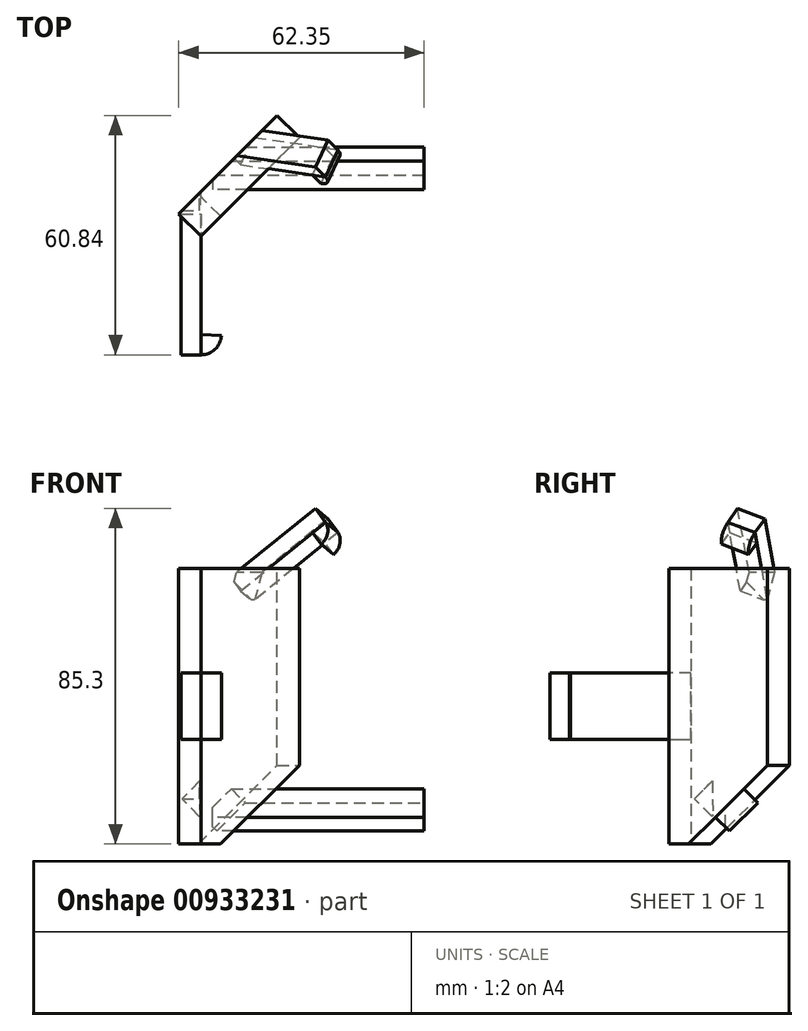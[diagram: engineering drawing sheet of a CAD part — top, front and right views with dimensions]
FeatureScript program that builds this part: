
annotation { "Feature Type Name" : "Feature", "Feature Type Description" : "" }
export const myFeature = defineFeature(function(context is Context, id is Id, definition is map)
    precondition{}
    {
        {
            var Q0;
            Q0=qCreatedBy(makeId("Top.planeOp"),FACE);
            var sketch = newSketch(context, id + "F0", { "sketchPlane" : qUnion([Q0])});
            skLineSegment(sketch, "E0.bottom", {"start": v(-25, 25) * mm, "end": v(25, 25) * mm});
            skLineSegment(sketch, "E0.top", {"start": v(-25, -25) * mm, "end": v(25, -25) * mm});
            skLineSegment(sketch, "E0.left", {"start": v(-25, 25) * mm, "end": v(-25, -25) * mm});
            skLineSegment(sketch, "E0.right", {"start": v(25, 25) * mm, "end": v(25, -25) * mm});
            skPoint(sketch, "E1", {"position": v(0, 25) * mm});
            skPoint(sketch, "E2", {"position": v(25, 0) * mm});
            skSolve(sketch);
        }
        {
            var Q0;
            Q0=qSketchRegion(id+"F0",true);
            extrude(context, id + "F1", {"entities" : qUnion([Q0]), "depth" : 80 * mm, "offsetDistance" : 25 * mm});
        }
        {
            var Q0;
            Q0=makeQuery(id+"F1.opExtrude","SWEPT_EDGE",EDGE,{"disambiguationData":[OSD([sQuery(id+"F0.wireOp",EDGE,"E0.top"),sQuery(id+"F0.wireOp",EDGE,"E0.right")])]});
            var Q1;
            Q1=makeQuery(id+"F1.opExtrude","CAP_EDGE",EDGE,{"disambiguationData":[OSD([sQuery(id+"F0.wireOp",EDGE,"E0.right")])],"isStart":false});
            var Q2;
            Q2=makeQuery(id+"F1.opExtrude","CAP_EDGE",EDGE,{"disambiguationData":[OSD([sQuery(id+"F0.wireOp",EDGE,"E0.top")])],"isStart":false});
            chamfer(context, id + "F2", {"entities" : qUnion([Q0, Q1, Q2]), "chamferType" : ChamferType.OFFSET_ANGLE, "width" : 20 * mm, "oppositeDirection" : false, "angle" : 50 * degree, "tangentPropagation" : true});
        }
        {
            var Q0;
            Q0=makeQuery(id+"F1.opExtrude","SWEPT_EDGE",EDGE,{"disambiguationData":[OSD([sQuery(id+"F0.wireOp",EDGE,"E0.bottom"),sQuery(id+"F0.wireOp",EDGE,"E0.left")])]});
            chamfer(context, id + "F3", {"entities" : qUnion([Q0]), "width" : 25 * mm, "tangentPropagation" : true});
        }
        {
            var Q0;
            {var subQ0=sQuery(id+"F0.wireOp",EDGE,"E0.left");var subQ1=sQuery(id+"F0.wireOp",EDGE,"E0.bottom");Q0=makeQuery(id+"F3.opChamfer","BLEND_EDGE",EDGE,{"blendedFrom":[makeQuery(id+"F1.opExtrude","SWEPT_EDGE",EDGE,{"disambiguationData":[OSD([subQ1,subQ0])]}),makeQuery(id+"F1.opExtrude","CAP_FACE",FACE,{"disambiguationData":[OSD([subQ1,sQuery(id+"F0.wireOp",EDGE,"E0.top"),subQ0,sQuery(id+"F0.wireOp",EDGE,"E0.right")])],"isStart":false})],"blendedInto":[makeQuery(id+"F1.opExtrude","CAP_FACE",FACE,{"disambiguationData":[OSD([subQ1,sQuery(id+"F0.wireOp",EDGE,"E0.top"),subQ0,sQuery(id+"F0.wireOp",EDGE,"E0.right")])],"isStart":false})]});}
            chamfer(context, id + "F4", {"entities" : qUnion([Q0]), "width" : 10 * mm, "tangentPropagation" : true});
        }
        {
            var Q0;
            Q0=makeQuery(id+"F1.opExtrude","CAP_EDGE",EDGE,{"disambiguationData":[OSD([sQuery(id+"F0.wireOp",EDGE,"E0.bottom")])],"isStart":true});
            var Q1;
            Q1=makeQuery(id+"F1.opExtrude","CAP_EDGE",EDGE,{"disambiguationData":[OSD([sQuery(id+"F0.wireOp",EDGE,"E0.top")])],"isStart":true});
            chamfer(context, id + "F5", {"entities" : qUnion([Q0, Q1]), "width" : 20 * mm, "tangentPropagation" : true});
        }
        {
            var Q0;
            Q0=makeQuery(id+"F3.opChamfer","BLEND_FACE",FACE,{"disambiguationData":[OSD([sQuery(id+"F0.wireOp",EDGE,"E0.bottom"),sQuery(id+"F0.wireOp",EDGE,"E0.left")])]});
            var sketch = newSketch(context, id + "F6", { "sketchPlane" : qUnion([Q0])});
            skLineSegment(sketch, "E3", {"start": v(17.68, 70) * mm, "end": v(17.68, 0) * mm});
            skLineSegment(sketch, "E4", {"start": v(17.68, 0) * mm, "end": v(10.6, 0) * mm});
            skLineSegment(sketch, "E5", {"start": v(10.6, 0) * mm, "end": v(-17.68, 20) * mm});
            skLineSegment(sketch, "E6", {"start": v(-17.68, 20) * mm, "end": v(-17.68, 70) * mm});
            skLineSegment(sketch, "E7", {"start": v(-17.68, 70) * mm, "end": v(17.68, 70) * mm});
            skSolve(sketch);
        }
        {
            var Q0;
            Q0=makeQuery(id+"F6.imprint","IMPRINT",FACE,{"disambiguationData":[TD([[makeQuery(id+"F6.imprint","IMPRINT",EDGE,{"derivedFrom":sQuery(id+"F6.wireOp",EDGE,"E3")}),-1.0]])]});
            cPlane(context, id + "F7", {"entities" : qUnion([Q0]), "cplaneType" : CPlaneType.OFFSET, "offset" : 0 * mm, "width" : 150 * mm, "height" : 150 * mm});
        }
        {
            var Q0;
            Q0=qCreatedBy(id+"F7.planeOp",FACE);
            var sketch = newSketch(context, id + "F8", { "sketchPlane" : qUnion([Q0])});
            skLineSegment(sketch, "E8", {"start": v(17.68, 70) * mm, "end": v(17.68, 0) * mm});
            skLineSegment(sketch, "E9", {"start": v(17.68, 0) * mm, "end": v(10.6, 0) * mm});
            skLineSegment(sketch, "E10", {"start": v(10.6, 0) * mm, "end": v(-17.68, 20) * mm});
            skLineSegment(sketch, "E11", {"start": v(-17.68, 20) * mm, "end": v(-17.68, 70) * mm});
            skLineSegment(sketch, "E12", {"start": v(-17.68, 70) * mm, "end": v(17.68, 70) * mm});
            skSolve(sketch);
        }
        {
            var Q0;
            Q0=qSketchRegion(id+"F8",true);
            extrude(context, id + "F9", {"entities" : qUnion([Q0]), "depth" : 8 * mm, "offsetDistance" : 25 * mm});
        }
        {
            var Q0;
            Q0=makeQuery(id+"F4.opChamfer","BLEND_FACE",FACE,{"disambiguationData":[OSD([sQuery(id+"F0.wireOp",EDGE,"E0.bottom"),sQuery(id+"F0.wireOp",EDGE,"E0.top"),sQuery(id+"F0.wireOp",EDGE,"E0.left"),sQuery(id+"F0.wireOp",EDGE,"E0.right")])]});
            cPlane(context, id + "F10", {"entities" : qUnion([Q0]), "cplaneType" : CPlaneType.OFFSET, "offset" : 0 * mm, "width" : 150 * mm, "height" : 150 * mm});
        }
        {
            var Q0;
            Q0=qCreatedBy(id+"F10.planeOp",FACE);
            var sketch = newSketch(context, id + "F11", { "sketchPlane" : qUnion([Q0])});
            skLineSegment(sketch, "E13", {"start": v(13.4, -29.38) * mm, "end": v(29.08, -48.84) * mm});
            skLineSegment(sketch, "E14", {"start": v(29.08, -48.84) * mm, "end": v(38.48, -41.27) * mm});
            skLineSegment(sketch, "E15", {"start": v(38.48, -41.27) * mm, "end": v(22.8, -21.8) * mm});
            skLineSegment(sketch, "E16", {"start": v(13.4, -29.38) * mm, "end": v(22.8, -21.8) * mm});
            skPoint(sketch, "E17", {"position": v(18.1, -25.59) * mm});
            skSolve(sketch);
        }
        {
            var Q0;
            Q0=makeQuery(id+"F1.opExtrude","SWEPT_FACE",FACE,{"disambiguationData":[OSD([sQuery(id+"F0.wireOp",EDGE,"E0.left")])]});
            cPlane(context, id + "F12", {"entities" : qUnion([Q0]), "cplaneType" : CPlaneType.OFFSET, "offset" : 0 * mm, "width" : 150 * mm, "height" : 150 * mm});
        }
        {
            var Q0;
            Q0=qCreatedBy(id+"F12.planeOp",FACE);
            var sketch = newSketch(context, id + "F13", { "sketchPlane" : qUnion([Q0])});
            skLineSegment(sketch, "E18", {"start": v(-5.66, 43.45) * mm, "end": v(30.18, 43.45) * mm});
            skLineSegment(sketch, "E19", {"start": v(30.18, 43.45) * mm, "end": v(30.18, 26.55) * mm});
            skLineSegment(sketch, "E20", {"start": v(30.18, 26.55) * mm, "end": v(-5.66, 26.55) * mm});
            skLineSegment(sketch, "E21", {"start": v(-5.66, 26.55) * mm, "end": v(-5.66, 43.45) * mm});
            skPoint(sketch, "E22", {"position": v(-5.66, 35) * mm});
            skSolve(sketch);
        }
        {
            var Q0;
            Q0=qSketchRegion(id+"F13",true);
            extrude(context, id + "F14", {"entities" : qUnion([Q0]), "depth" : 5 * mm, "offsetDistance" : 25 * mm});
        }
        {
            var Q0;
            Q0=makeQuery(id+"F1.opExtrude","CAP_FACE",FACE,{"disambiguationData":[OSD([sQuery(id+"F0.wireOp",EDGE,"E0.bottom"),sQuery(id+"F0.wireOp",EDGE,"E0.top"),sQuery(id+"F0.wireOp",EDGE,"E0.left"),sQuery(id+"F0.wireOp",EDGE,"E0.right")])],"isStart":true});
            cPlane(context, id + "F15", {"entities" : qUnion([Q0]), "cplaneType" : CPlaneType.OFFSET, "offset" : 0 * mm, "width" : 150 * mm, "height" : 150 * mm});
        }
        {
            var Q0;
            Q0=qCreatedBy(id+"F15.planeOp",FACE);
            var sketch = newSketch(context, id + "F16", { "sketchPlane" : qUnion([Q0])});
            skLineSegment(sketch, "E23", {"start": v(-30.03, -6.76) * mm, "end": v(-14.64, 9.79) * mm});
            skLineSegment(sketch, "E24", {"start": v(-30.03, -6.76) * mm, "end": v(-25.94, -10.56) * mm});
            skLineSegment(sketch, "E25", {"start": v(-25.94, -10.56) * mm, "end": v(-10.56, 5.99) * mm});
            skLineSegment(sketch, "E26", {"start": v(-10.56, 5.99) * mm, "end": v(-14.64, 9.79) * mm});
            skSolve(sketch);
        }
        {
            var Q0;
            Q0=makeQuery(id+"F5.opChamfer","BLEND_FACE",FACE,{"disambiguationData":[OSD([sQuery(id+"F0.wireOp",EDGE,"E0.bottom")])]});
            var sketch = newSketch(context, id + "F17", { "sketchPlane" : qUnion([Q0])});
            skLineSegment(sketch, "E27", {"start": v(22, 23.4) * mm, "end": v(-31.69, 23.4) * mm});
            skLineSegment(sketch, "E28", {"start": v(-31.69, 23.4) * mm, "end": v(-31.69, 13.2) * mm});
            skLineSegment(sketch, "E29", {"start": v(-31.69, 13.2) * mm, "end": v(22, 13.2) * mm});
            skLineSegment(sketch, "E30", {"start": v(22, 13.2) * mm, "end": v(22, 23.4) * mm});
            skSolve(sketch);
        }
        {
            var Q0;
            Q0=qSketchRegion(id+"F17",true);
            extrude(context, id + "F18", {"entities" : qUnion([Q0]), "depth" : 5 * mm, "offsetDistance" : 25 * mm});
        }
        {
            var Q0;
            Q0=makeQuery(id+"F14.opExtrude","SWEPT_FACE",FACE,{"disambiguationData":[OSD([sQuery(id+"F13.wireOp",EDGE,"E20")])]});
            var sketch = newSketch(context, id + "F19", { "sketchPlane" : qUnion([Q0])});
            skArc(sketch, "E31", {"start": v(-19.8, 25.22) * mm, "mid": v(-21.4, 28.74) * mm, "end": v(-25, 30.18) * mm});
            skLineSegment(sketch, "E32", {"start": v(-25, 30.18) * mm, "end": v(-25, 24.96) * mm});
            skLineSegment(sketch, "E33", {"start": v(-19.8, 25.22) * mm, "end": v(-25, 24.96) * mm});
            skSolve(sketch);
        }
        {
            var Q0;
            Q0=qSketchRegion(id+"F19",true);
            extrude(context, id + "F20", {"entities" : qUnion([Q0]), "oppositeDirection" : true, "depth" : 17 * mm, "offsetDistance" : 25 * mm});
        }
        {
            var Q0;
            Q0=makeQuery(id+"F9.opExtrude","CAP_FACE",FACE,{"disambiguationData":[OSD([sQuery(id+"F8.wireOp",EDGE,"E8"),sQuery(id+"F8.wireOp",EDGE,"E9"),sQuery(id+"F8.wireOp",EDGE,"E10"),sQuery(id+"F8.wireOp",EDGE,"E11"),sQuery(id+"F8.wireOp",EDGE,"E12")])],"isStart":false});
            var sketch = newSketch(context, id + "F21", { "sketchPlane" : qUnion([Q0])});
            skLineSegment(sketch, "E34", {"start": v(6.42, 2.96) * mm, "end": v(-6.89, 12.37) * mm});
            skLineSegment(sketch, "E35", {"start": v(-6.89, 12.37) * mm, "end": v(4.32, 20) * mm});
            skLineSegment(sketch, "E36", {"start": v(4.32, 20) * mm, "end": v(6.42, 2.96) * mm});
            skSolve(sketch);
        }
        {
            var Q0;
            Q0=qSketchRegion(id+"F21",true);
            extrude(context, id + "F22", {"entities" : qUnion([Q0]), "operationType" : NewBodyOperationType.REMOVE, "endBound" : BoundingType.THROUGH_ALL, "depth" : 25 * mm, "offsetDistance" : 25 * mm});
        }
        {
            var Q0;
            Q0=makeQuery(id+"F18.opExtrude","SWEPT_FACE",FACE,{"disambiguationData":[OSD([sQuery(id+"F17.wireOp",EDGE,"E27")])]});
            var sketch = newSketch(context, id + "F23", { "sketchPlane" : qUnion([Q0])});
            skArc(sketch, "E37", {"start": v(25.12, -2.7) * mm, "mid": v(29.65, -0.94) * mm, "end": v(31.53, 3.54) * mm});
            skLineSegment(sketch, "E38", {"start": v(31.53, 3.54) * mm, "end": v(25.3, 3.53) * mm});
            skLineSegment(sketch, "E39", {"start": v(25.12, -2.7) * mm, "end": v(25.3, 3.53) * mm});
            skSolve(sketch);
        }
        {
            var Q0;
            Q0=qSketchRegion(id+"F23",true);
            extrude(context, id + "F24", {"entities" : qUnion([Q0]), "oppositeDirection" : true, "depth" : 10.7 * mm, "offsetDistance" : 25 * mm});
        }
        {
            var Q0;
            Q0=makeQuery(id+"F4.opChamfer","BLEND_FACE",FACE,{"disambiguationData":[OSD([sQuery(id+"F0.wireOp",EDGE,"E0.bottom"),sQuery(id+"F0.wireOp",EDGE,"E0.top"),sQuery(id+"F0.wireOp",EDGE,"E0.left"),sQuery(id+"F0.wireOp",EDGE,"E0.right")])]});
            var sketch = newSketch(context, id + "F25", { "sketchPlane" : qUnion([Q0])});
            skLineSegment(sketch, "E40", {"start": v(14.93, -55.46) * mm, "end": v(14.93, -26.52) * mm});
            skLineSegment(sketch, "E41", {"start": v(6.93, -26.52) * mm, "end": v(6.93, -55.46) * mm});
            skLineSegment(sketch, "E42", {"start": v(14.93, -55.46) * mm, "end": v(6.93, -55.46) * mm});
            skLineSegment(sketch, "E43", {"start": v(14.93, -26.52) * mm, "end": v(6.93, -26.52) * mm});
            skLineSegment(sketch, "E44", {"start": v(18.6, -22.34) * mm, "end": v(43.44, -34.97) * mm});
            skLineSegment(sketch, "E45", {"start": v(18.6, -22.34) * mm, "end": v(22.23, -15.2) * mm});
            skLineSegment(sketch, "E46", {"start": v(47.07, -27.84) * mm, "end": v(22.23, -15.2) * mm});
            skLineSegment(sketch, "E47", {"start": v(47.07, -27.84) * mm, "end": v(43.44, -34.97) * mm});
            skSolve(sketch);
        }
        {
            var Q0;
            Q0 = qSketchRegion(id + "F25", true);
            extrude(context, id + "F26", {"entities" : qUnion([Q0]), "depth" : 5 * mm, "offsetDistance" : 25 * mm});
        }
        {
            var Q0;
            Q0=makeQuery(id+"F26.opExtrude","SWEPT_FACE",FACE,{"disambiguationData":[OSD([sQuery(id+"F25.wireOp",EDGE,"E46")])]});
            var sketch = newSketch(context, id + "F27", { "sketchPlane" : qUnion([Q0])});
            skArc(sketch, "E48", {"start": v(-12.1, 81.7) * mm, "mid": v(-12.68, 78.58) * mm, "end": v(-10.9, 75.95) * mm});
            skLineSegment(sketch, "E49", {"start": v(-12.1, 81.7) * mm, "end": v(-8.6, 79.43) * mm});
            skLineSegment(sketch, "E50", {"start": v(-10.9, 75.95) * mm, "end": v(-8.6, 79.43) * mm});
            skSolve(sketch);
        }
        {
            var Q0;
            Q0 = qSketchRegion(id + "F27", true);
            extrude(context, id + "F28", {"entities" : qUnion([Q0]), "oppositeDirection" : true, "depth" : 8 * mm, "offsetDistance" : 25 * mm});
        }
        {
            var Q0;
            Q0=makeQuery(id+"F26.opExtrude","SWEPT_FACE",FACE,{"disambiguationData":[OSD([sQuery(id+"F25.wireOp",EDGE,"E40")])]});
            var sketch = newSketch(context, id + "F29", { "sketchPlane" : qUnion([Q0])});
            skArc(sketch, "E51", {"start": v(-14.92, 81.84) * mm, "mid": v(-15.25, 78.53) * mm, "end": v(-12.85, 76.22) * mm});
            skLineSegment(sketch, "E52", {"start": v(-11.67, 79.84) * mm, "end": v(-12.85, 76.22) * mm});
            skLineSegment(sketch, "E53", {"start": v(-11.67, 79.84) * mm, "end": v(-14.92, 81.84) * mm});
            skSolve(sketch);
        }
        {
            var Q0;
            Q0 = qSketchRegion(id + "F29", true);
            extrude(context, id + "F30", {"entities" : qUnion([Q0]), "operationType" : NewBodyOperationType.ADD, "oppositeDirection" : true, "depth" : 8 * mm, "offsetDistance" : 25 * mm});
        }
        {
            var Q0;
            Q0=makeQuery(id+"F1.opExtrude","SWEPT_BODY",BODY,{"disambiguationData":[OSD([sQuery(id+"F0.wireOp",EDGE,"E0.bottom"),sQuery(id+"F0.wireOp",EDGE,"E0.top"),sQuery(id+"F0.wireOp",EDGE,"E0.left"),sQuery(id+"F0.wireOp",EDGE,"E0.right")])]});
            deleteBodies(context, id + "F31", {"entities" : qUnion([Q0])});
        }
        {
            var Q0;
            Q0=makeQuery(id+"F9.opExtrude","CAP_FACE",FACE,{"disambiguationData":[OSD([sQuery(id+"F8.wireOp",EDGE,"E8"),sQuery(id+"F8.wireOp",EDGE,"E9"),sQuery(id+"F8.wireOp",EDGE,"E10"),sQuery(id+"F8.wireOp",EDGE,"E11"),sQuery(id+"F8.wireOp",EDGE,"E12")])],"isStart":false});
            var sketch = newSketch(context, id + "F32", { "sketchPlane" : qUnion([Q0])});
            skLineSegment(sketch, "E54.bottom", {"start": v(-28.6, 75.04) * mm, "end": v(25.26, 75.04) * mm});
            skLineSegment(sketch, "E54.top", {"start": v(-28.6, -3.81) * mm, "end": v(25.26, -3.81) * mm});
            skLineSegment(sketch, "E54.left", {"start": v(-28.6, 75.04) * mm, "end": v(-28.6, -3.81) * mm});
            skLineSegment(sketch, "E54.right", {"start": v(25.26, 75.04) * mm, "end": v(25.26, -3.81) * mm});
            skSolve(sketch);
        }
        {
            var Q0;
            Q0 = qSketchRegion(id + "F32", true);
            extrude(context, id + "F33", {"entities" : qUnion([Q0]), "operationType" : NewBodyOperationType.REMOVE, "depth" : 25 * mm, "offsetDistance" : 25 * mm});
        }
    });
